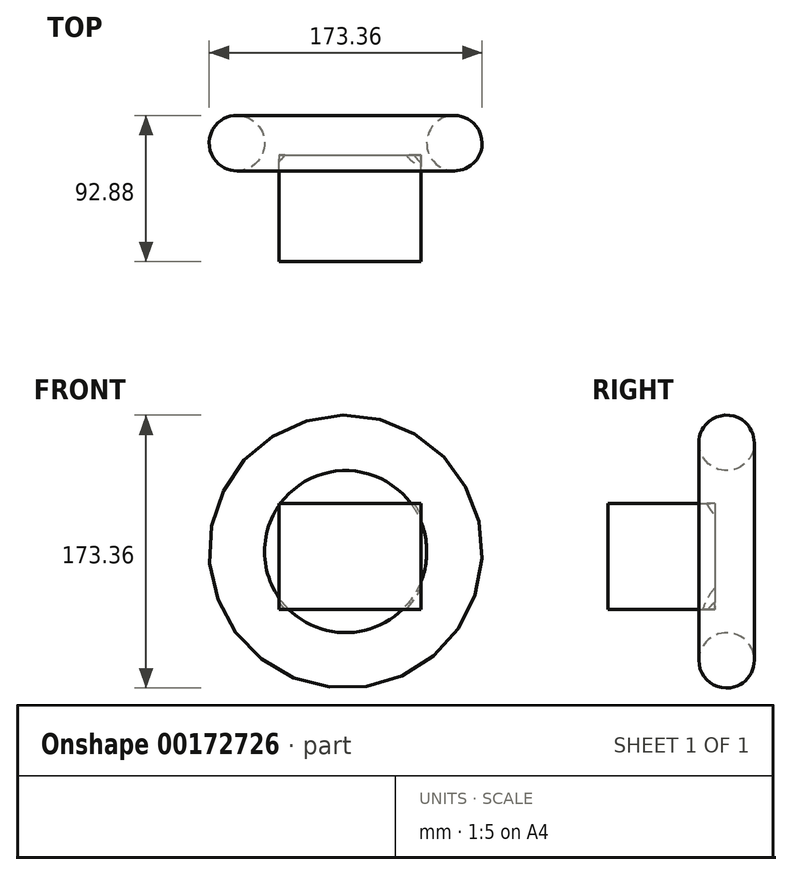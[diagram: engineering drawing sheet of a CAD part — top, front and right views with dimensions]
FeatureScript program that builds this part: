
annotation { "Feature Type Name" : "Feature", "Feature Type Description" : "" }
export const myFeature = defineFeature(function(context is Context, id is Id, definition is map)
    precondition{}
    {
        {
            var Q0;
            Q0=qCreatedBy(makeId("Front.planeOp"),FACE);
            var sketch = newSketch(context, id + "F0", { "sketchPlane" : qUnion([Q0])});
            skLineSegment(sketch, "E0.bottom", {"start": v(-42.34, 30.45) * mm, "end": v(47.86, 30.45) * mm});
            skLineSegment(sketch, "E0.top", {"start": v(-42.34, -36.62) * mm, "end": v(47.86, -36.62) * mm});
            skLineSegment(sketch, "E0.left", {"start": v(-42.34, 30.45) * mm, "end": v(-42.34, -36.62) * mm});
            skLineSegment(sketch, "E0.right", {"start": v(47.86, 30.45) * mm, "end": v(47.86, -36.62) * mm});
            skSolve(sketch);
        }
        {
            var Q0;
            Q0=makeQuery(id+"F0.imprint","IMPRINT",FACE,{"disambiguationData":[TD([[makeQuery(id+"F0.imprint","IMPRINT",EDGE,{"derivedFrom":sQuery(id+"F0.wireOp",EDGE,"E0.bottom")}),-1.0]])]});
            extrude(context, id + "F1", {"entities" : qUnion([Q0]), "depth" : 67.82 * mm});
        }
        {
            var Q0;
            Q0=qCreatedBy(makeId("Top.planeOp"),FACE);
            var sketch = newSketch(context, id + "F2", { "sketchPlane" : qUnion([Q0])});
            skCircle(sketch, "E1", {"center": v(-69.08, 7.47) * mm, "radius": 17.6 * mm});
            skSolve(sketch);
        }
        {
            var Q0;
            Q0=qCreatedBy(makeId("Top.planeOp"),FACE);
            var sketch = newSketch(context, id + "F3", { "sketchPlane" : qUnion([Q0])});
            skLineSegment(sketch, "E2", {"start": v(0, 69) * mm, "end": v(0, -104.62) * mm, "construction": true});
            skSolve(sketch);
        }
        {
            var Q0;
            Q0=makeQuery(id+"F2.imprint","IMPRINT",FACE,{"disambiguationData":[TD([[makeQuery(id+"F2.imprint","IMPRINT",EDGE,{"derivedFrom":sQuery(id+"F2.wireOp",EDGE,"E1")}),1.0]])]});
            var Q1;
            Q1=sQuery(id+"F3.wireOp",EDGE,"E2");
            revolve(context, id + "F4", {"operationType" : NewBodyOperationType.ADD, "entities" : qUnion([Q0]), "axis" : qUnion([Q1]), "revolveType" : RevolveType.FULL});
        }
    });
